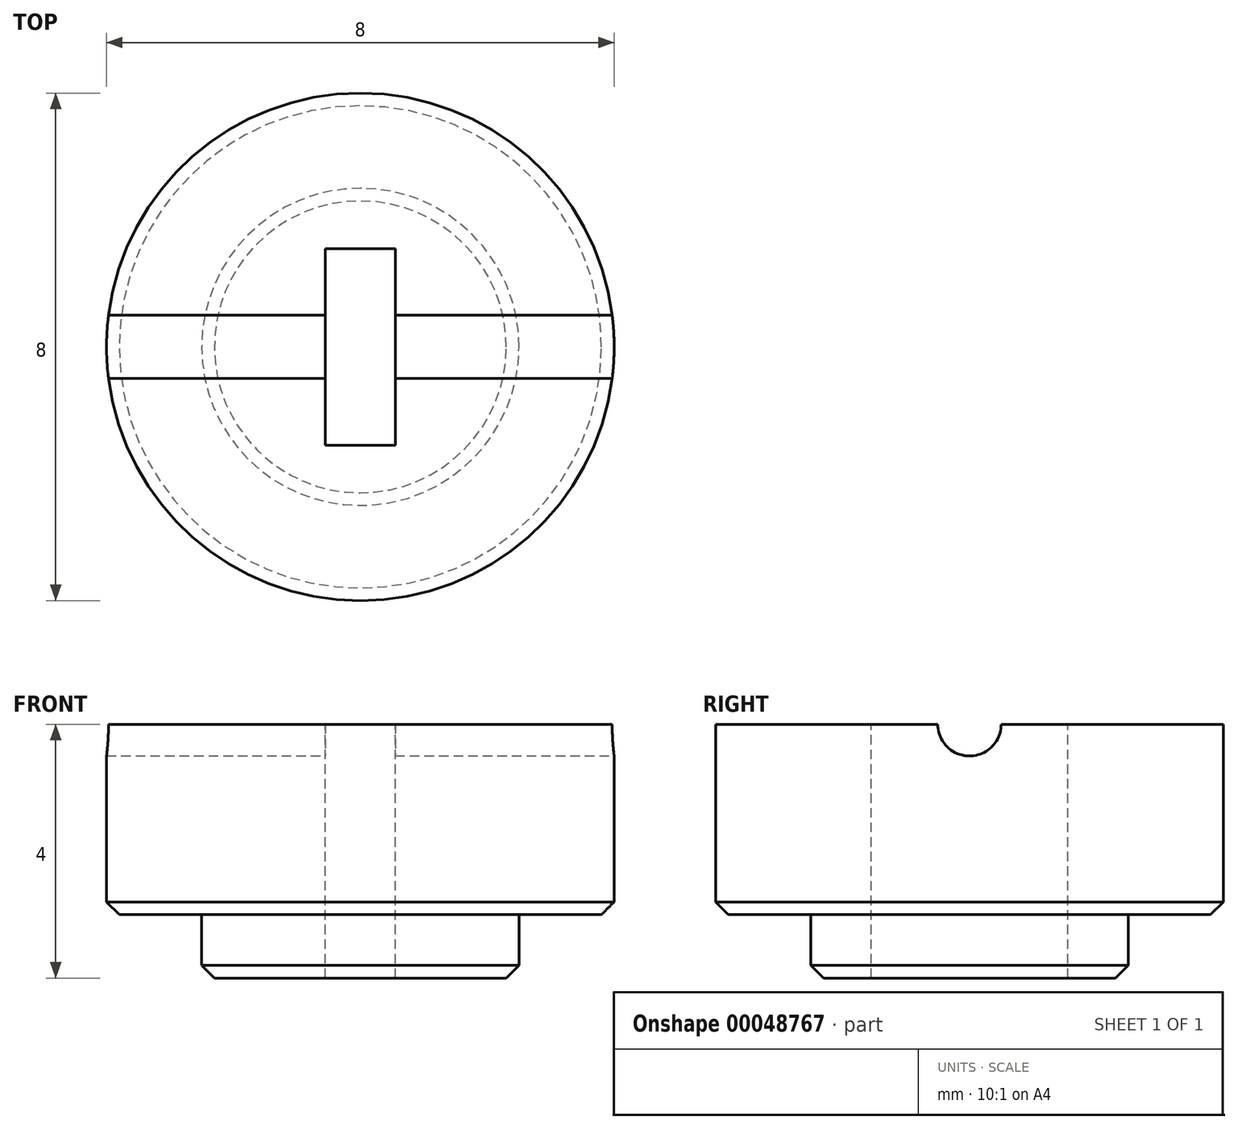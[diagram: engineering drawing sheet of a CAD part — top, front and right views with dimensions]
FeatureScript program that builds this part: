
annotation { "Feature Type Name" : "Feature", "Feature Type Description" : "" }
export const myFeature = defineFeature(function(context is Context, id is Id, definition is map)
    precondition{}
    {
        {
            var Q0;
            Q0=qCreatedBy(makeId("Top.planeOp"),FACE);
            var sketch = newSketch(context, id + "F0", { "sketchPlane" : qUnion([Q0])});
            skCircle(sketch, "E0", {"center": v(0, 0) * mm, "radius": 4 * mm});
            skSolve(sketch);
        }
        {
            var Q0;
            Q0=makeQuery(id+"F0.imprint","IMPRINT",FACE,{"disambiguationData":[TD([[makeQuery(id+"F0.imprint","IMPRINT",EDGE,{"derivedFrom":sQuery(id+"F0.wireOp",EDGE,"E0")}),1.0]])]});
            extrude(context, id + "F1", {"entities" : qUnion([Q0]), "oppositeDirection" : true, "depth" : 3 * mm});
        }
        {
            var Q0;
            Q0=makeQuery(id+"F1.opExtrude","CAP_FACE",FACE,{"disambiguationData":[OSD([sQuery(id+"F0.wireOp",EDGE,"E0")])],"isStart":false});
            var sketch = newSketch(context, id + "F2", { "sketchPlane" : qUnion([Q0])});
            skCircle(sketch, "E1", {"center": v(0, 0) * mm, "radius": 2.5 * mm});
            skSolve(sketch);
        }
        {
            var Q0;
            Q0=makeQuery(id+"F2.imprint","IMPRINT",FACE,{"disambiguationData":[TD([[makeQuery(id+"F2.imprint","IMPRINT",EDGE,{"derivedFrom":sQuery(id+"F2.wireOp",EDGE,"E1")}),1.0]])]});
            extrude(context, id + "F3", {"entities" : qUnion([Q0]), "operationType" : NewBodyOperationType.ADD, "depth" : 1 * mm});
        }
        {
            var Q0;
            Q0=qCreatedBy(makeId("Right.planeOp"),FACE);
            var sketch = newSketch(context, id + "F4", { "sketchPlane" : qUnion([Q0])});
            skPoint(sketch, "E2.middle", {"position": v(0, 0) * mm});
            skCircle(sketch, "E3", {"center": v(0, 0) * mm, "radius": 0.5 * mm});
            skSolve(sketch);
        }
        {
            var Q0;
            Q0=makeQuery(id+"F4.imprint","IMPRINT",FACE,{"disambiguationData":[TD([[makeQuery(id+"F4.imprint","IMPRINT",EDGE,{"derivedFrom":sQuery(id+"F4.wireOp",EDGE,"E3")}),1.0]])]});
            extrude(context, id + "F5", {"entities" : qUnion([Q0]), "operationType" : NewBodyOperationType.REMOVE, "oppositeDirection" : true, "depth" : 18 * mm, "symmetric" : true});
        }
        {
            var Q0;
            Q0=makeQuery(id+"F1.opExtrude","CAP_FACE",FACE,{"disambiguationData":[OSD([sQuery(id+"F0.wireOp",EDGE,"E0")])],"isStart":true});
            var sketch = newSketch(context, id + "F6", { "sketchPlane" : qUnion([Q0])});
            skLineSegment(sketch, "E4.bottom", {"start": v(0.55, -1.55) * mm, "end": v(-0.55, -1.55) * mm});
            skLineSegment(sketch, "E4.top", {"start": v(0.55, 1.55) * mm, "end": v(-0.55, 1.55) * mm});
            skLineSegment(sketch, "E4.left", {"start": v(0.55, -1.55) * mm, "end": v(0.55, 1.55) * mm});
            skLineSegment(sketch, "E4.right", {"start": v(-0.55, -1.55) * mm, "end": v(-0.55, 1.55) * mm});
            skPoint(sketch, "E4.middle", {"position": v(0, 0) * mm});
            skSolve(sketch);
        }
        {
            var Q0;
            Q0=makeQuery(id+"F6.imprint","IMPRINT",FACE,{"disambiguationData":[TD([[makeQuery(id+"F6.imprint","IMPRINT",EDGE,{"derivedFrom":sQuery(id+"F6.wireOp",EDGE,"E4.bottom")}),-1.0]])]});
            var Q1;
            {var subQ0=sQuery(id+"F6.wireOp",EDGE,"E4.left");var subQ1=makeQuery(id+"F5.boolean.opBoolean","COPY",EDGE,{"derivedFrom":makeQuery(id+"F5.opExtrude","CAP_EDGE",EDGE,{"disambiguationData":[OSD([sQuery(id+"F4.wireOp",EDGE,"E2.bottom")])],"isStart":true})});var subQ2=makeQuery(id+"F6.imprint","INTERSECT",VERTEX,{"derivedFrom":[subQ1,subQ0]});Q1=makeQuery(id+"F6.imprint","IMPRINT",FACE,{"disambiguationData":[TD([[makeQuery(id+"F6.imprint","IMPRINT",EDGE,{"disambiguationData":[TD([[subQ2,-1.0]])],"derivedFrom":subQ0}),1.0]])]});}
            var Q2;
            {var subQ0=sQuery(id+"F6.wireOp",EDGE,"E4.top");Q2=makeQuery(id+"F6.imprint","IMPRINT",FACE,{"disambiguationData":[TD([[makeQuery(id+"F6.imprint","IMPRINT",EDGE,{"derivedFrom":subQ0}),1.0]])]});}
            extrude(context, id + "F7", {"entities" : qUnion([Q0, Q1, Q2]), "operationType" : NewBodyOperationType.REMOVE, "endBound" : BoundingType.THROUGH_ALL, "oppositeDirection" : true, "depth" : 25 * mm});
        }
        {
            var Q0;
            Q0=makeQuery(id+"F1.opExtrude","CAP_EDGE",EDGE,{"disambiguationData":[OSD([sQuery(id+"F0.wireOp",EDGE,"E0")])],"isStart":false});
            var Q1;
            Q1=makeQuery(id+"F3.opExtrude","CAP_EDGE",EDGE,{"disambiguationData":[OSD([sQuery(id+"F2.wireOp",EDGE,"E1")])],"isStart":false});
            chamfer(context, id + "F8", {"entities" : qUnion([Q0, Q1]), "width" : 0.2 * mm, "tangentPropagation" : true});
        }
    });
